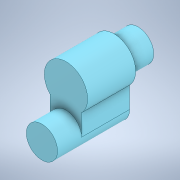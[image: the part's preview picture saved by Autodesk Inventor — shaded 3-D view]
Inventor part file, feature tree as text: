
AUTODESK INVENTOR PART (.ipt)
format: ipt  version: 2022 (Build 260153000, 153)  size: 136,192 bytes
history: native  units: in
note: dims shown in document units (in); Inventor stores cm internally (conversion verified against a paired STEP export)
features: extrude x3, sketch x2
ambient origin geometry x8: Origin, YZ Plane, XZ Plane, XY Plane, X Axis, Y Axis, Z Axis, Center Point
bodies: Solid1 (feature_tree)
feature tree (5):
  sketch  "Sketch2"  dims[d0=0.1969in d1=0.0in]
  extrude  "Extrusion1"  TaperAngle=0.0deg  [1 undecoded]
  extrude  "Extrusion2"  Depth=0.1969in TaperAngle=0.0deg
  extrude  "Extrusion3"  Depth=0.2559in
  sketch  "Sketch3"  dims[d2=0.3937in d3=0.0in d4=0.1969in d5=0.0in d6=0.2559in d8=0.3543in d9=0.2953in d7=0.0197in d10=0.0344in]
note: 1 required parameter value undecoded (feature->parameter linkage not recoverable at this tier; creation-order binding heuristic only, values carry confidence <= 0.55)
